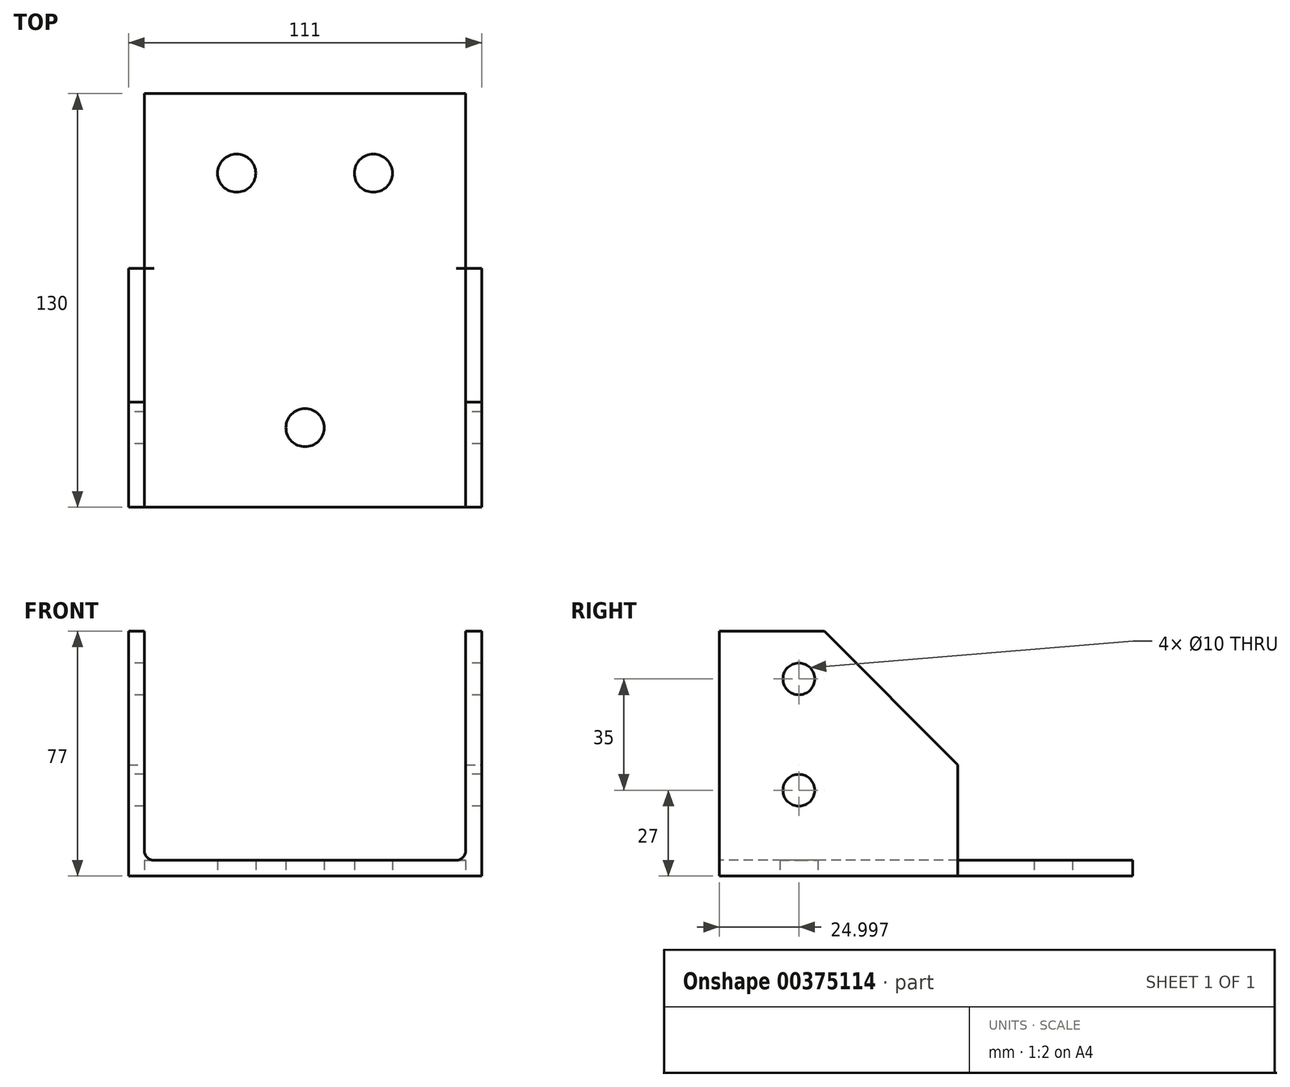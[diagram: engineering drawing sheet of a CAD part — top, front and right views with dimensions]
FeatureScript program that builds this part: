
annotation { "Feature Type Name" : "Feature", "Feature Type Description" : "" }
export const myFeature = defineFeature(function(context is Context, id is Id, definition is map)
    precondition{}
    {
        {
            var Q0;
            Q0=qCreatedBy(makeId("Top.planeOp"),FACE);
            var sketch = newSketch(context, id + "F0", { "sketchPlane" : qUnion([Q0])});
            skLineSegment(sketch, "E0", {"start": v(-53.77, -56.5) * mm, "end": v(57.23, -56.5) * mm});
            skLineSegment(sketch, "E1", {"start": v(57.23, -56.5) * mm, "end": v(57.23, 18.5) * mm});
            skLineSegment(sketch, "E2", {"start": v(57.23, 18.5) * mm, "end": v(52.23, 18.5) * mm});
            skLineSegment(sketch, "E3", {"start": v(52.23, 18.5) * mm, "end": v(52.23, 73.5) * mm});
            skLineSegment(sketch, "E4", {"start": v(52.23, 73.5) * mm, "end": v(-48.77, 73.5) * mm});
            skLineSegment(sketch, "E5", {"start": v(-48.77, 73.5) * mm, "end": v(-48.77, 18.5) * mm});
            skLineSegment(sketch, "E6", {"start": v(-48.77, 18.5) * mm, "end": v(-53.77, 18.5) * mm});
            skLineSegment(sketch, "E7", {"start": v(-53.77, 18.5) * mm, "end": v(-53.77, -56.5) * mm});
            skLineSegment(sketch, "E8", {"start": v(-48.77, 18.5) * mm, "end": v(52.23, 18.5) * mm});
            skLineSegment(sketch, "E9", {"start": v(57.23, -56.5) * mm, "end": v(57.23, -30.82) * mm});
            skLineSegment(sketch, "E10", {"start": v(57.23, -56.5) * mm, "end": v(1.73, -56.5) * mm});
            skLineSegment(sketch, "E11", {"start": v(1.73, -56.5) * mm, "end": v(1.73, -31.5) * mm});
            skCircle(sketch, "E12", {"center": v(1.73, -31.5) * mm, "radius": 6 * mm});
            skLineSegment(sketch, "E13", {"start": v(52.23, 73.5) * mm, "end": v(23.23, 73.5) * mm});
            skLineSegment(sketch, "E14", {"start": v(52.23, 73.5) * mm, "end": v(-19.77, 73.5) * mm});
            skLineSegment(sketch, "E15", {"start": v(23.23, 73.5) * mm, "end": v(23.23, 48.5) * mm});
            skLineSegment(sketch, "E16", {"start": v(-19.77, 73.5) * mm, "end": v(-19.77, 48.5) * mm});
            skCircle(sketch, "E17", {"center": v(-19.77, 48.5) * mm, "radius": 6 * mm});
            skCircle(sketch, "E18", {"center": v(23.23, 48.5) * mm, "radius": 6 * mm});
            skSolve(sketch);
        }
        {
            var Q0;
            Q0=makeQuery(id+"F0.imprint","IMPRINT",FACE,{"disambiguationData":[TD([[makeQuery(id+"F0.imprint","IMPRINT",EDGE,{"derivedFrom":sQuery(id+"F0.wireOp",EDGE,"E0")}),1.0]])]});
            extrude(context, id + "F1", {"entities" : qUnion([Q0]), "depth" : 77 * mm});
        }
        {
            var Q0;
            {var subQ1=sQuery(id+"F0.wireOp",EDGE,"E3");Q0=makeQuery(id+"F0.imprint","IMPRINT",FACE,{"disambiguationData":[TD([[makeQuery(id+"F0.imprint","IMPRINT",EDGE,{"derivedFrom":subQ1}),1.0]])]});}
            extrude(context, id + "F2", {"entities" : qUnion([Q0]), "operationType" : NewBodyOperationType.ADD, "depth" : 5 * mm});
        }
        {
            var Q0;
            Q0=makeQuery(id+"F1.opExtrude","CAP_EDGE",EDGE,{"disambiguationData":[OSD([sQuery(id+"F0.wireOp",EDGE,"E2"),sQuery(id+"F0.wireOp",EDGE,"E6"),sQuery(id+"F0.wireOp",EDGE,"E8")])],"isStart":false});
            chamfer(context, id + "F3", {"entities" : qUnion([Q0]), "width" : 42 * mm, "tangentPropagation" : true});
        }
        {
            var Q0;
            Q0=makeQuery(id+"F1.opExtrude","SWEPT_FACE",FACE,{"disambiguationData":[OSD([sQuery(id+"F0.wireOp",EDGE,"E7")])]});
            var sketch = newSketch(context, id + "F4", { "sketchPlane" : qUnion([Q0])});
            skLineSegment(sketch, "E19", {"start": v(56.5, 77) * mm, "end": v(56.5, 62) * mm});
            skLineSegment(sketch, "E20", {"start": v(56.5, 62) * mm, "end": v(56.5, 27) * mm});
            skLineSegment(sketch, "E21", {"start": v(56.5, 27) * mm, "end": v(31.5, 27) * mm});
            skLineSegment(sketch, "E22", {"start": v(56.5, 62) * mm, "end": v(31.5, 62) * mm});
            skCircle(sketch, "E23", {"center": v(31.5, 27) * mm, "radius": 5 * mm});
            skCircle(sketch, "E24", {"center": v(31.5, 62) * mm, "radius": 5 * mm});
            skSolve(sketch);
        }
        {
            var Q0;
            Q0=makeQuery(id+"F4.imprint","IMPRINT",FACE,{"disambiguationData":[TD([[makeQuery(id+"F4.imprint","IMPRINT",EDGE,{"derivedFrom":sQuery(id+"F4.wireOp",EDGE,"E23")}),1.0]])]});
            var Q1;
            Q1=makeQuery(id+"F4.imprint","IMPRINT",FACE,{"disambiguationData":[TD([[makeQuery(id+"F4.imprint","IMPRINT",EDGE,{"derivedFrom":sQuery(id+"F4.wireOp",EDGE,"E24")}),1.0]])]});
            extrude(context, id + "F5", {"entities" : qUnion([Q0, Q1]), "operationType" : NewBodyOperationType.REMOVE, "oppositeDirection" : true, "depth" : 1000 * mm});
        }
        {
            var Q0;
            Q0=makeQuery(id+"F1.opExtrude","SWEPT_FACE",FACE,{"disambiguationData":[OSD([sQuery(id+"F0.wireOp",EDGE,"E0"),sQuery(id+"F0.wireOp",EDGE,"E10")])]});
            var sketch = newSketch(context, id + "F6", { "sketchPlane" : qUnion([Q0])});
            skLineSegment(sketch, "E25", {"start": v(-48.77, 77) * mm, "end": v(-48.77, 8) * mm});
            skLineSegment(sketch, "E26", {"start": v(-45.77, 5) * mm, "end": v(49.23, 5) * mm});
            skLineSegment(sketch, "E27", {"start": v(52.23, 8) * mm, "end": v(52.23, 77) * mm});
            skPoint(sketch, "E28.end.orphan", {"position": v(-53.77, 5) * mm});
            skPoint(sketch, "E28.start.orphan", {"position": v(-53.77, 0) * mm});
            skPoint(sketch, "E29.orphan", {"position": v(-48.77, 0) * mm});
            skPoint(sketch, "E30.end.orphan", {"position": v(52.23, 0) * mm});
            skPoint(sketch, "E30.start.orphan", {"position": v(57.23, 0) * mm});
            skPoint(sketch, "E31.start.orphan", {"position": v(-53.77, 77) * mm});
            skLineSegment(sketch, "E32", {"start": v(57.23, 77) * mm, "end": v(57.23, 8) * mm});
            skLineSegment(sketch, "E33", {"start": v(-53.77, 77) * mm, "end": v(-53.77, 8) * mm});
            skLineSegment(sketch, "E34", {"start": v(49.23, 0) * mm, "end": v(-45.77, 0) * mm});
            skLineSegment(sketch, "E35", {"start": v(-48.77, 77) * mm, "end": v(-53.77, 77) * mm});
            skLineSegment(sketch, "E36", {"start": v(57.23, 77) * mm, "end": v(52.23, 77) * mm});
            skPoint(sketch, "E37.visualSharp", {"position": v(52.23, 5) * mm});
            skArc(sketch, "E37.filletArc", {"start": v(49.23, 5) * mm, "mid": v(51.35, 5.88) * mm, "end": v(52.23, 8) * mm});
            skPoint(sketch, "E38.visualSharp", {"position": v(-48.77, 5) * mm});
            skArc(sketch, "E38.filletArc", {"start": v(-48.77, 8) * mm, "mid": v(-47.89, 5.88) * mm, "end": v(-45.77, 5) * mm});
            skArc(sketch, "E39.filletArc", {"start": v(49.23, 0) * mm, "mid": v(54.89, 2.34) * mm, "end": v(57.23, 8) * mm});
            skArc(sketch, "E40.filletArc", {"start": v(-53.77, 8) * mm, "mid": v(-51.42, 2.34) * mm, "end": v(-45.77, 0) * mm});
            skSolve(sketch);
        }
        {
            var Q0;
            {var subQ1=sQuery(id+"F6.wireOp",EDGE,"E25");Q0=makeQuery(id+"F6.imprint","IMPRINT",FACE,{"disambiguationData":[TD([[makeQuery(id+"F6.imprint","IMPRINT",EDGE,{"derivedFrom":subQ1}),1.0]])]});}
            extrude(context, id + "F7", {"entities" : qUnion([Q0]), "operationType" : NewBodyOperationType.REMOVE, "oppositeDirection" : true, "depth" : 10000 * mm});
        }
    });
